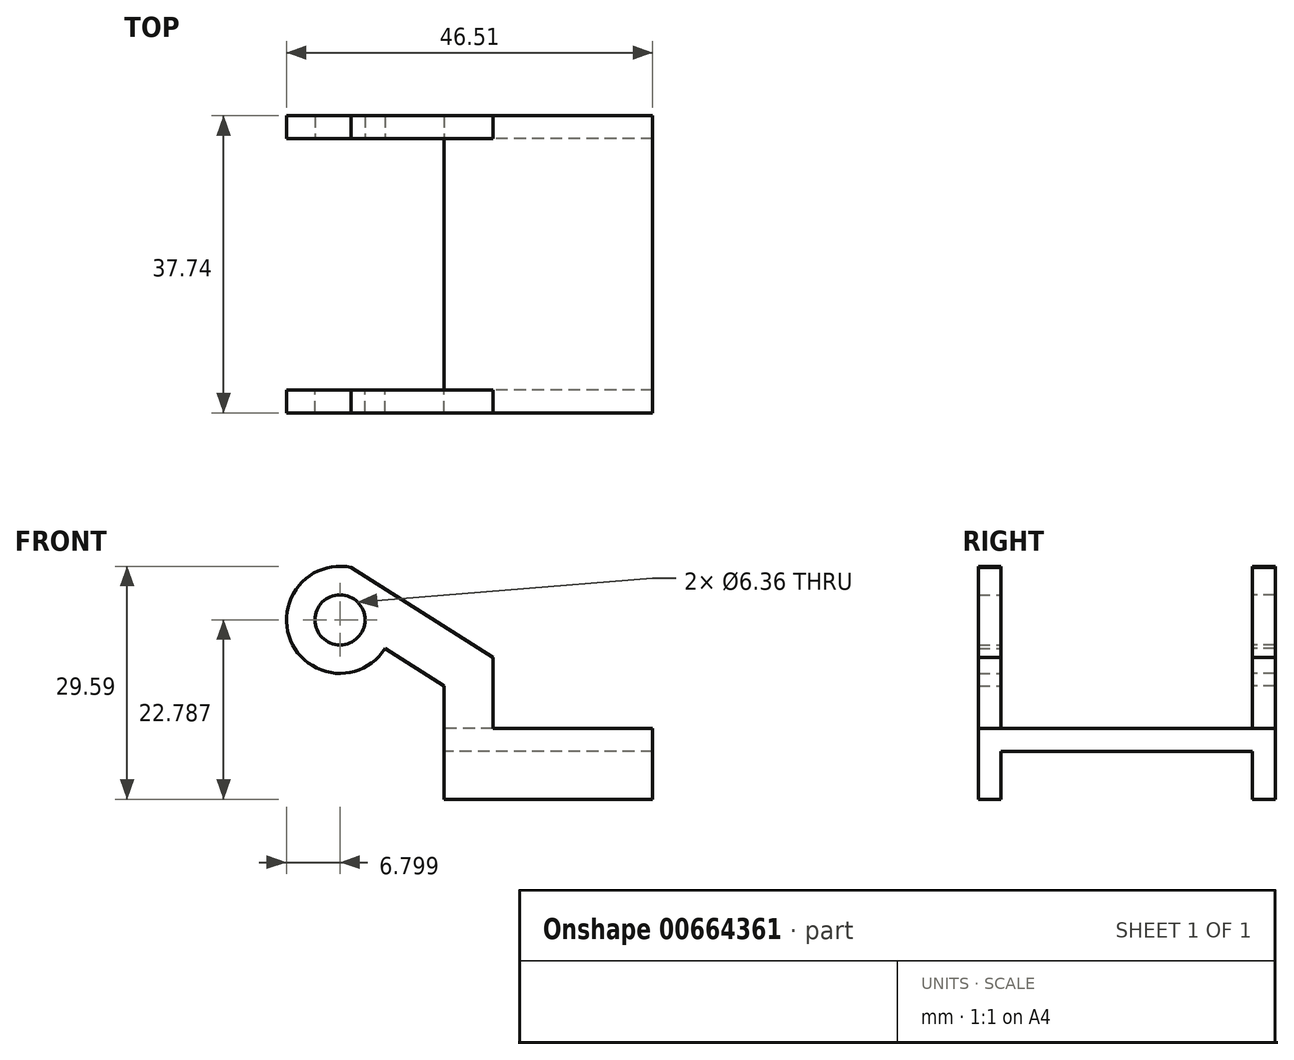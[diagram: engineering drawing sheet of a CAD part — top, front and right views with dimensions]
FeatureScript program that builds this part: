
annotation { "Feature Type Name" : "Feature", "Feature Type Description" : "" }
export const myFeature = defineFeature(function(context is Context, id is Id, definition is map)
    precondition{}
    {
        {
            var Q0;
            Q0=qCreatedBy(makeId("Front.planeOp"),FACE);
            var sketch = newSketch(context, id + "F0", { "sketchPlane" : qUnion([Q0])});
            skLineSegment(sketch, "E0", {"start": v(26.51, 0) * mm, "end": v(26.51, 9) * mm});
            skLineSegment(sketch, "E1", {"start": v(26.51, 9) * mm, "end": v(6.23, 9) * mm});
            skLineSegment(sketch, "E2", {"start": v(6.23, 9) * mm, "end": v(6.23, 18) * mm});
            skLineSegment(sketch, "E3", {"start": v(0, 14.4) * mm, "end": v(0, 0) * mm});
            skLineSegment(sketch, "E4", {"start": v(0, 0) * mm, "end": v(26.51, 0) * mm});
            skCircle(sketch, "E5", {"center": v(-13.2, 22.79) * mm, "radius": 3.18 * mm});
            skArc(sketch, "E6", {"start": v(-11.76, 29.43) * mm, "mid": v(-19.47, 20.16) * mm, "end": v(-7.46, 19.14) * mm});
            skLineSegment(sketch, "E7", {"start": v(0, 14.4) * mm, "end": v(-7.46, 19.14) * mm});
            skLineSegment(sketch, "E8", {"start": v(6.23, 18) * mm, "end": v(-11.76, 29.43) * mm});
            skSolve(sketch);
        }
        {
            var Q0;
            Q0=makeQuery(id+"F0.imprint","IMPRINT",FACE,{"disambiguationData":[TD([[makeQuery(id+"F0.imprint","IMPRINT",EDGE,{"derivedFrom":sQuery(id+"F0.wireOp",EDGE,"E0")}),1.0]])]});
            extrude(context, id + "F1", {"entities" : qUnion([Q0]), "depth" : 2.9 * mm, "offsetDistance" : 25 * mm});
        }
        {
            var Q0;
            Q0=makeQuery(id+"F1.opExtrude","CAP_FACE",FACE,{"disambiguationData":[OSD([sQuery(id+"F0.wireOp",EDGE,"E0"),sQuery(id+"F0.wireOp",EDGE,"E1"),sQuery(id+"F0.wireOp",EDGE,"E2"),sQuery(id+"F0.wireOp",EDGE,"E3"),sQuery(id+"F0.wireOp",EDGE,"E4"),sQuery(id+"F0.wireOp",EDGE,"E5"),sQuery(id+"F0.wireOp",EDGE,"E6"),sQuery(id+"F0.wireOp",EDGE,"E7"),sQuery(id+"F0.wireOp",EDGE,"E8")])],"isStart":false});
            var sketch = newSketch(context, id + "F2", { "sketchPlane" : qUnion([Q0])});
            skLineSegment(sketch, "E9", {"start": v(6.23, 9) * mm, "end": v(26.51, 9) * mm});
            skLineSegment(sketch, "E10", {"start": v(26.51, 9) * mm, "end": v(26.51, 6.1) * mm});
            skLineSegment(sketch, "E11", {"start": v(26.51, 6.1) * mm, "end": v(0, 6.1) * mm});
            skLineSegment(sketch, "E12", {"start": v(0, 6.1) * mm, "end": v(0, 9) * mm});
            skLineSegment(sketch, "E13", {"start": v(0, 9) * mm, "end": v(6.23, 9) * mm});
            skSolve(sketch);
        }
        {
            var Q0;
            Q0 = qSketchRegion(id + "F2", true);
            extrude(context, id + "F3", {"entities" : qUnion([Q0]), "operationType" : NewBodyOperationType.ADD, "oppositeDirection" : true, "depth" : 18.87 * mm, "offsetDistance" : 25 * mm});
        }
        {
            var Q0;
            Q0=qCreatedBy(makeId("Front.planeOp"),FACE);
            cPlane(context, id + "F4", {"entities" : qUnion([Q0]), "cplaneType" : CPlaneType.OFFSET, "offset" : 15.97 * mm, "oppositeDirection" : true, "width" : 150 * mm, "height" : 150 * mm});
        }
        {
            var Q0;
            Q0=makeQuery(id+"F1.opExtrude","SWEPT_BODY",BODY,{"disambiguationData":[OSD([sQuery(id+"F0.wireOp",EDGE,"E0"),sQuery(id+"F0.wireOp",EDGE,"E1"),sQuery(id+"F0.wireOp",EDGE,"E2"),sQuery(id+"F0.wireOp",EDGE,"E3"),sQuery(id+"F0.wireOp",EDGE,"E4"),sQuery(id+"F0.wireOp",EDGE,"E5"),sQuery(id+"F0.wireOp",EDGE,"E6"),sQuery(id+"F0.wireOp",EDGE,"E7"),sQuery(id+"F0.wireOp",EDGE,"E8")])]});
            var Q1;
            Q1=qCreatedBy(id+"F4.planeOp",FACE);
            mirror(context, id + "F5", {"operationType" : NewBodyOperationType.ADD, "entities" : qUnion([Q0]), "mirrorPlane" : qUnion([Q1])});
        }
    });
